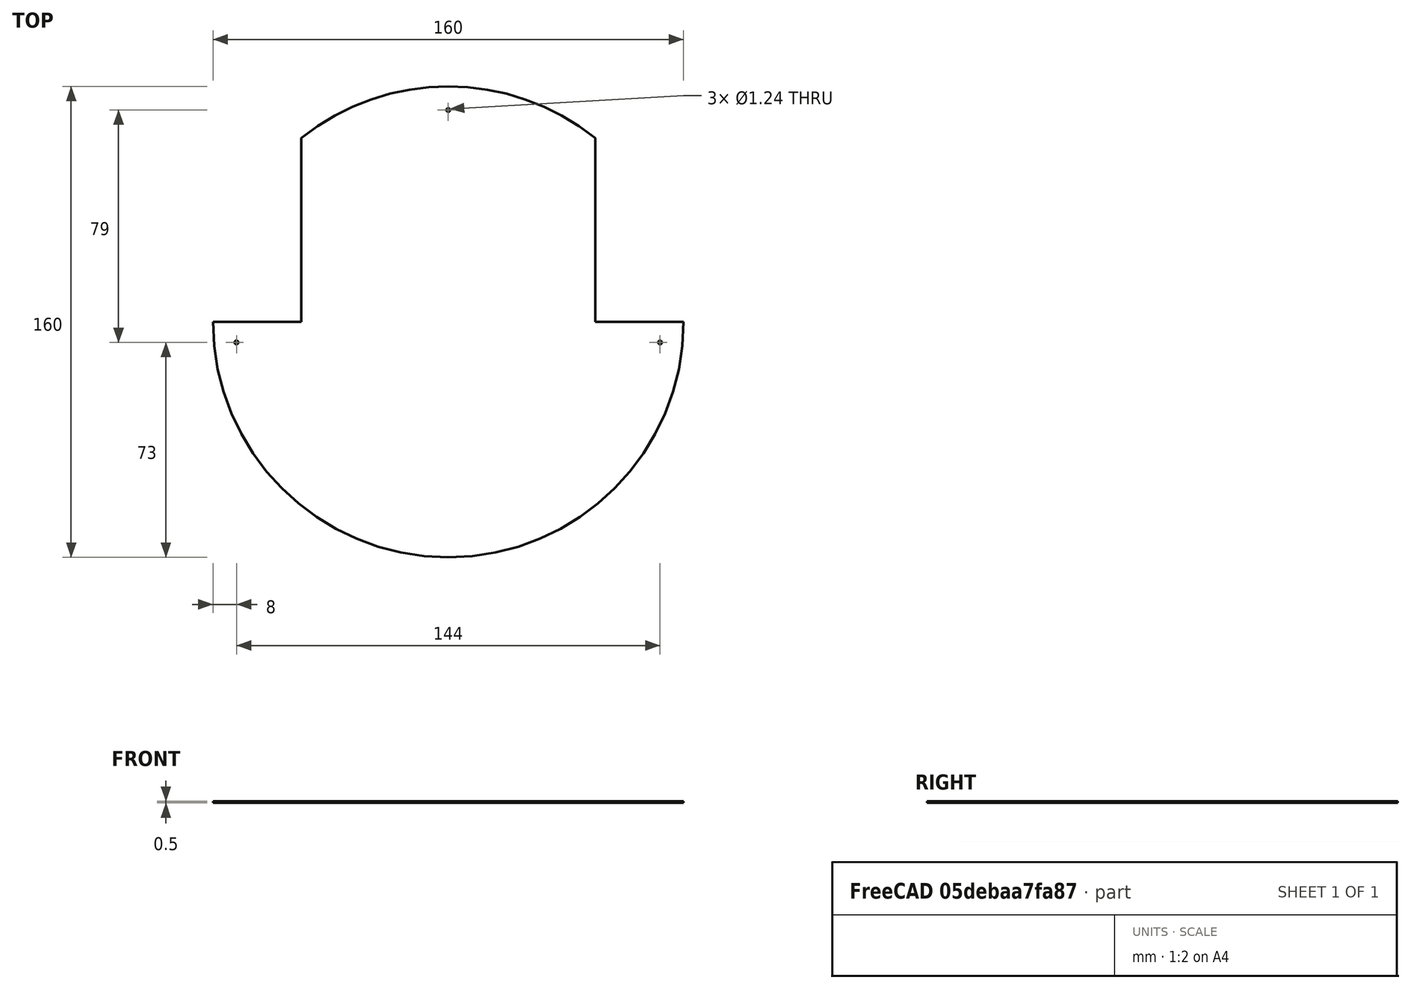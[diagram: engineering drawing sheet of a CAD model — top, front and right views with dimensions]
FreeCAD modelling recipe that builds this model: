
FCSTD DOCUMENT  (FreeCAD 0.16R6706 (Git))
Label: Base
License: All rights reserved
LicenseURL: http://en.wikipedia.org/wiki/All_rights_reserved
objects: Part::Cut×5, Part::Cylinder×4, Part::Box×2
note: 11 computed .brp shape members not serialized (recipe doc carries the construction recipe); baked Part::Feature solids carry a one-line shape summary decoded from their .brp

FEATURE [Part::Cylinder] Cylinder  label="Cilindro"
  Angle = 360
  Height = 0.5
  Radius = 80
FEATURE [Part::Cylinder] Cylinder001  label="PERFO"
  Angle = 360
  Height = 0.5
  Placement = pos=(0,72,0) rot=(0,0,1;0rad)
  Radius = 0.62
FEATURE [Part::Cylinder] Cylinder003  label="PERFO002"
  Angle = 360
  Height = 0.5
  Placement = pos=(-72,-7,0) rot=(0,0,1;0rad)
  Radius = 0.62
FEATURE [Part::Box] Box  label="Cubo"
  Height = 0.5
  Length = 30
  Placement = pos=(-80,0,0) rot=(0,0,1;0rad)
  Width = 70
FEATURE [Part::Box] Box001  label="Cubo001"
  Height = 0.5
  Length = 30
  Placement = pos=(50,0,0) rot=(0,0,1;0rad)
  Width = 70
FEATURE [Part::Cylinder] Cylinder004  label="PERFO003"
  Angle = 360
  Height = 0.5
  Placement = pos=(72,-7,0) rot=(0,0,1;0rad)
  Radius = 0.62
FEATURE [Part::Cut] Cut
  Base = -> Cylinder
  Tool = -> Cylinder001
FEATURE [Part::Cut] Cut001
  Base = -> Cut
  Tool = -> Cylinder003
FEATURE [Part::Cut] Cut002
  Base = -> Cut001
  Tool = -> Cylinder004
FEATURE [Part::Cut] Cut003
  Base = -> Cut002
  Tool = -> Box001
FEATURE [Part::Cut] Cut004
  Base = -> Cut003
  Tool = -> Box
